# Revit family: P400229-031
name_source: partatom
category: Lighting Fixtures
revit_build: Autodesk Revit 2014 (Build: 20130308_1515(x64)
units: mm (PartAtom-declared; Revit-internal decimal feet)

## types (1)
- P400229-031
    Apparent Load = 60 VA
    Assembly Code = D5020200
    Connector = Polycarbonate, Smoke
    Default Elevation = 48 "
    Description = Create an extension of your personality and lifestyle with the rustic charm of this island light. Country character is the cornerstone of this light fixture that features a crate-like frame composed of aged oak. Black barn-inspired metal details complete this must-have farmhouse design.
    Features = Country character is the cornerstone of this light fixture that features a crate-like frame composed of aged oak.
Black barn-inspired metal details complete this must-have farmhouse design.
Create an extension of your personality and lifestyle with the rustic charm of this island light.
Ideal for any dining room, kitchen, or foyer.
Perfect for urban industrial, rustic, farmhouse, or coastal settings.
Measures 36-inch width by 7.87-inch height.
Uses four medium base bulbs that are sold separately (60w max - LED or incandescent).
Able to be fully dimmable with dimmable bulbs.
Includes installation instructions and mounting hardware.
Progress Lighting products are designed for exceptional quality, reliability, and functionality.
    Fixture distribution = Direct
    Glass = Paint - Hubbell - White Texture
    Gold = Hubbell - Gold
    Height = 9.25 "
    Housing Material = Paint - Hubbell - Textured Camera Black
    Lamp = LED or Medium Base
    Load Classification = Lighting
    Manufacturer = Progress Lighting
    Model = P400229-031
    Power Factor = 1
    Product Documentation Link = https://hubbellcdn.com
    Product Link = https://www.hubbell.com
    URL = https://www.hubbell.com
    Voltage = 120 V
    Warranty = 1 year Warranty
    Wattage Comments = 60W
    Watts = 60 W
    Width = 6 "
    Wood = Wood Planks

## geometry (parser evidence)
native form markers: Sweep x6
no freeform markers — native parametric forms only
